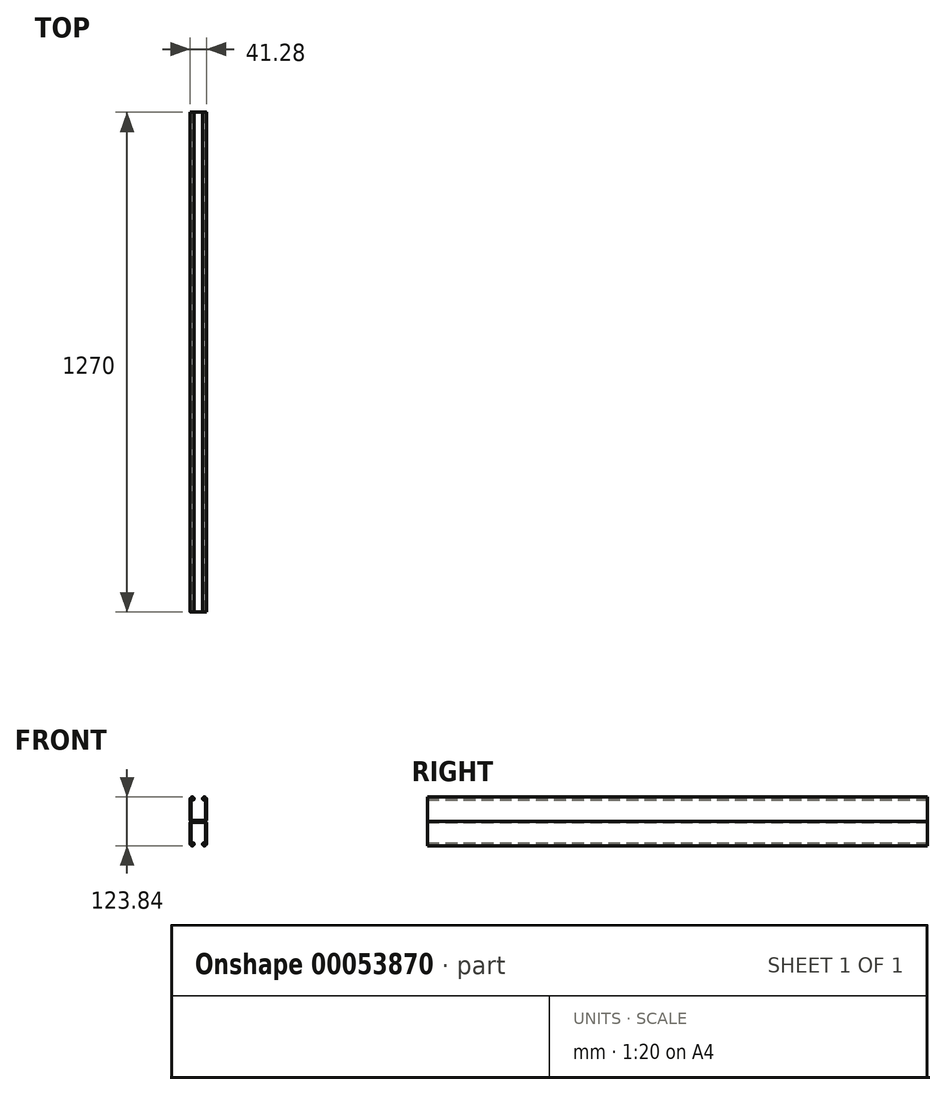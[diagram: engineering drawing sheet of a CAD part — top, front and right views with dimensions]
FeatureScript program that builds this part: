
annotation { "Feature Type Name" : "Feature", "Feature Type Description" : "" }
export const myFeature = defineFeature(function(context is Context, id is Id, definition is map)
    precondition{}
    {
        {
            var Q0;
            Q0=qCreatedBy(makeId("Front.planeOp"),FACE);
            var sketch = newSketch(context, id + "F0", { "sketchPlane" : qUnion([Q0])});
            skLineSegment(sketch, "E0", {"start": v(-72.96, 0) * mm, "end": v(72.4, 0) * mm});
            skLineSegment(sketch, "E1", {"start": v(0, -67.32) * mm, "end": v(0, 85.39) * mm});
            skArc(sketch, "E2.0", {"start": v(20.64, 56.86) * mm, "mid": v(19.16, 60.44) * mm, "end": v(15.59, 61.92) * mm});
            skFitSpline(sketch, "E2.1", {"points": [v(20.64, 3.46) * mm, v(20.64, 21.26) * mm, v(20.64, 39.06) * mm, v(20.64, 56.86) * mm]});
            skArc(sketch, "E2.2", {"start": v(17.33, 0) * mm, "mid": v(19.68, 1.07) * mm, "end": v(20.64, 3.46) * mm});
            skArc(sketch, "E2.3", {"start": v(20.64, -3.46) * mm, "mid": v(19.68, -1.07) * mm, "end": v(17.33, 0) * mm});
            skFitSpline(sketch, "E2.4", {"points": [v(20.64, -56.86) * mm, v(20.64, -39.06) * mm, v(20.64, -21.26) * mm, v(20.64, -3.46) * mm]});
            skArc(sketch, "E2.5", {"start": v(15.59, -61.92) * mm, "mid": v(19.16, -60.44) * mm, "end": v(20.64, -56.86) * mm});
            skFitSpline(sketch, "E2.6", {"points": [v(14.57, -61.92) * mm, v(14.91, -61.92) * mm, v(15.25, -61.92) * mm, v(15.59, -61.92) * mm]});
            skArc(sketch, "E2.7", {"start": v(11.1, -58.45) * mm, "mid": v(12.12, -60.9) * mm, "end": v(14.57, -61.92) * mm});
            skArc(sketch, "E2.8", {"start": v(-15.59, 61.92) * mm, "mid": v(-19.16, 60.44) * mm, "end": v(-20.64, 56.86) * mm});
            skFitSpline(sketch, "E2.9", {"points": [v(-14.57, 61.92) * mm, v(-14.91, 61.92) * mm, v(-15.25, 61.92) * mm, v(-15.59, 61.92) * mm]});
            skArc(sketch, "E2.10", {"start": v(-11.1, 58.45) * mm, "mid": v(-12.12, 60.9) * mm, "end": v(-14.57, 61.92) * mm});
            skFitSpline(sketch, "E2.11", {"points": [v(-11.1, 56.1) * mm, v(-11.1, 56.89) * mm, v(-11.1, 57.67) * mm, v(-11.1, 58.45) * mm]});
            skArc(sketch, "E2.12", {"start": v(-13.78, 56.1) * mm, "mid": v(-12.45, 54.77) * mm, "end": v(-11.1, 56.1) * mm});
            skFitSpline(sketch, "E2.13", {"points": [v(-13.78, 58.45) * mm, v(-13.78, 57.67) * mm, v(-13.78, 56.89) * mm, v(-13.78, 56.1) * mm]});
            skArc(sketch, "E2.14", {"start": v(-14.57, 59.24) * mm, "mid": v(-14.01, 59.01) * mm, "end": v(-13.78, 58.45) * mm});
            skFitSpline(sketch, "E2.15", {"points": [v(-15.59, 59.24) * mm, v(-15.25, 59.24) * mm, v(-14.91, 59.24) * mm, v(-14.57, 59.24) * mm]});
            skArc(sketch, "E2.16", {"start": v(-17.97, 56.86) * mm, "mid": v(-17.27, 58.55) * mm, "end": v(-15.59, 59.24) * mm});
            skFitSpline(sketch, "E2.17", {"points": [v(-17.97, 56.86) * mm, v(-17.97, 39.06) * mm, v(-17.97, 21.26) * mm, v(-17.97, 3.46) * mm]});
            skArc(sketch, "E2.18", {"start": v(-17.18, 2.67) * mm, "mid": v(-17.74, 2.9) * mm, "end": v(-17.97, 3.46) * mm});
            skFitSpline(sketch, "E2.19", {"points": [v(17.18, 2.67) * mm, v(5.73, 2.67) * mm, v(-5.73, 2.67) * mm, v(-17.18, 2.67) * mm]});
            skArc(sketch, "E2.20", {"start": v(11.1, 56.1) * mm, "mid": v(12.45, 54.77) * mm, "end": v(13.78, 56.1) * mm});
            skFitSpline(sketch, "E2.21", {"points": [v(11.1, 58.45) * mm, v(11.1, 57.67) * mm, v(11.1, 56.89) * mm, v(11.1, 56.1) * mm]});
            skArc(sketch, "E2.22", {"start": v(14.57, 61.92) * mm, "mid": v(12.12, 60.9) * mm, "end": v(11.1, 58.45) * mm});
            skFitSpline(sketch, "E2.23", {"points": [v(15.59, 61.92) * mm, v(15.25, 61.92) * mm, v(14.91, 61.92) * mm, v(14.57, 61.92) * mm]});
            skFitSpline(sketch, "E2.24", {"points": [v(13.78, 56.1) * mm, v(13.78, 56.89) * mm, v(13.78, 57.67) * mm, v(13.78, 58.45) * mm]});
            skArc(sketch, "E2.25", {"start": v(13.78, 58.45) * mm, "mid": v(14.01, 59.01) * mm, "end": v(14.57, 59.24) * mm});
            skFitSpline(sketch, "E2.26", {"points": [v(14.57, 59.24) * mm, v(14.91, 59.24) * mm, v(15.25, 59.24) * mm, v(15.59, 59.24) * mm]});
            skArc(sketch, "E2.27", {"start": v(15.59, 59.24) * mm, "mid": v(17.27, 58.55) * mm, "end": v(17.97, 56.86) * mm});
            skFitSpline(sketch, "E2.28", {"points": [v(17.97, 56.86) * mm, v(17.97, 39.06) * mm, v(17.97, 21.26) * mm, v(17.97, 3.46) * mm]});
            skArc(sketch, "E2.29", {"start": v(17.97, 3.46) * mm, "mid": v(17.74, 2.9) * mm, "end": v(17.18, 2.67) * mm});
            skFitSpline(sketch, "E2.30", {"points": [v(-20.64, 56.86) * mm, v(-20.64, 39.06) * mm, v(-20.64, 21.26) * mm, v(-20.64, 3.46) * mm]});
            skArc(sketch, "E2.31", {"start": v(-20.64, 3.46) * mm, "mid": v(-19.68, 1.07) * mm, "end": v(-17.33, 0) * mm});
            skArc(sketch, "E2.32", {"start": v(-17.33, 0) * mm, "mid": v(-19.68, -1.07) * mm, "end": v(-20.64, -3.46) * mm});
            skFitSpline(sketch, "E2.33", {"points": [v(-20.64, -3.46) * mm, v(-20.64, -21.26) * mm, v(-20.64, -39.06) * mm, v(-20.64, -56.86) * mm]});
            skArc(sketch, "E2.34", {"start": v(-20.64, -56.86) * mm, "mid": v(-19.16, -60.44) * mm, "end": v(-15.59, -61.92) * mm});
            skFitSpline(sketch, "E2.35", {"points": [v(-15.59, -61.92) * mm, v(-15.25, -61.92) * mm, v(-14.91, -61.92) * mm, v(-14.57, -61.92) * mm]});
            skArc(sketch, "E2.36", {"start": v(-14.57, -61.92) * mm, "mid": v(-12.12, -60.9) * mm, "end": v(-11.1, -58.45) * mm});
            skFitSpline(sketch, "E2.37", {"points": [v(-11.1, -58.45) * mm, v(-11.1, -57.67) * mm, v(-11.1, -56.89) * mm, v(-11.1, -56.1) * mm]});
            skArc(sketch, "E2.38", {"start": v(-11.1, -56.1) * mm, "mid": v(-12.45, -54.77) * mm, "end": v(-13.78, -56.1) * mm});
            skFitSpline(sketch, "E2.39", {"points": [v(-13.78, -56.1) * mm, v(-13.78, -56.89) * mm, v(-13.78, -57.67) * mm, v(-13.78, -58.45) * mm]});
            skArc(sketch, "E2.40", {"start": v(-13.78, -58.45) * mm, "mid": v(-14.01, -59.01) * mm, "end": v(-14.57, -59.24) * mm});
            skFitSpline(sketch, "E2.41", {"points": [v(-14.57, -59.24) * mm, v(-14.91, -59.24) * mm, v(-15.25, -59.24) * mm, v(-15.59, -59.24) * mm]});
            skArc(sketch, "E2.42", {"start": v(-15.59, -59.24) * mm, "mid": v(-17.27, -58.55) * mm, "end": v(-17.97, -56.86) * mm});
            skFitSpline(sketch, "E2.43", {"points": [v(-17.97, -56.86) * mm, v(-17.97, -39.06) * mm, v(-17.97, -21.26) * mm, v(-17.97, -3.46) * mm]});
            skArc(sketch, "E2.44", {"start": v(-17.97, -3.46) * mm, "mid": v(-17.74, -2.9) * mm, "end": v(-17.18, -2.67) * mm});
            skFitSpline(sketch, "E2.45", {"points": [v(-17.18, -2.67) * mm, v(-5.73, -2.67) * mm, v(5.73, -2.67) * mm, v(17.18, -2.67) * mm]});
            skArc(sketch, "E2.46", {"start": v(17.18, -2.67) * mm, "mid": v(17.74, -2.9) * mm, "end": v(17.97, -3.46) * mm});
            skFitSpline(sketch, "E2.47", {"points": [v(17.97, -3.46) * mm, v(17.97, -21.26) * mm, v(17.97, -39.06) * mm, v(17.97, -56.86) * mm]});
            skArc(sketch, "E2.48", {"start": v(17.97, -56.86) * mm, "mid": v(17.27, -58.55) * mm, "end": v(15.59, -59.24) * mm});
            skFitSpline(sketch, "E2.49", {"points": [v(15.59, -59.24) * mm, v(15.25, -59.24) * mm, v(14.91, -59.24) * mm, v(14.57, -59.24) * mm]});
            skArc(sketch, "E2.50", {"start": v(14.57, -59.24) * mm, "mid": v(14.01, -59.01) * mm, "end": v(13.78, -58.45) * mm});
            skFitSpline(sketch, "E2.51", {"points": [v(13.78, -58.45) * mm, v(13.78, -57.67) * mm, v(13.78, -56.89) * mm, v(13.78, -56.1) * mm]});
            skArc(sketch, "E2.52", {"start": v(13.78, -56.1) * mm, "mid": v(12.45, -54.77) * mm, "end": v(11.1, -56.1) * mm});
            skFitSpline(sketch, "E2.53", {"points": [v(11.1, -56.1) * mm, v(11.1, -56.89) * mm, v(11.1, -57.67) * mm, v(11.1, -58.45) * mm]});
            skSolve(sketch);
        }
        {
            var Q0;
            Q0=makeQuery(id+"F0.imprint","IMPRINT",FACE,{"disambiguationData":[TD([[makeQuery(id+"F0.imprint","IMPRINT",EDGE,{"derivedFrom":sQuery(id+"F0.wireOp",EDGE,"E2.0")}),1.0]])]});
            var Q1;
            {var subQ6=sQuery(id+"F0.wireOp",EDGE,"E2.3");Q1=makeQuery(id+"F0.imprint","IMPRINT",FACE,{"disambiguationData":[TD([[makeQuery(id+"F0.imprint","IMPRINT",EDGE,{"derivedFrom":subQ6}),1.0]])]});}
            var Q2;
            Q2=makeQuery(id+"F0.imprint","IMPRINT",FACE,{"disambiguationData":[TD([[makeQuery(id+"F0.imprint","IMPRINT",EDGE,{"derivedFrom":sQuery(id+"F0.wireOp",EDGE,"E2.8")}),1.0]])]});
            var Q3;
            {var subQ4=sQuery(id+"F0.wireOp",EDGE,"E2.32");Q3=makeQuery(id+"F0.imprint","IMPRINT",FACE,{"disambiguationData":[TD([[makeQuery(id+"F0.imprint","IMPRINT",EDGE,{"derivedFrom":subQ4}),1.0]])]});}
            extrude(context, id + "F1", {"entities" : qUnion([Q0, Q1, Q2, Q3]), "depth" : 1270 * mm});
        }
    });
